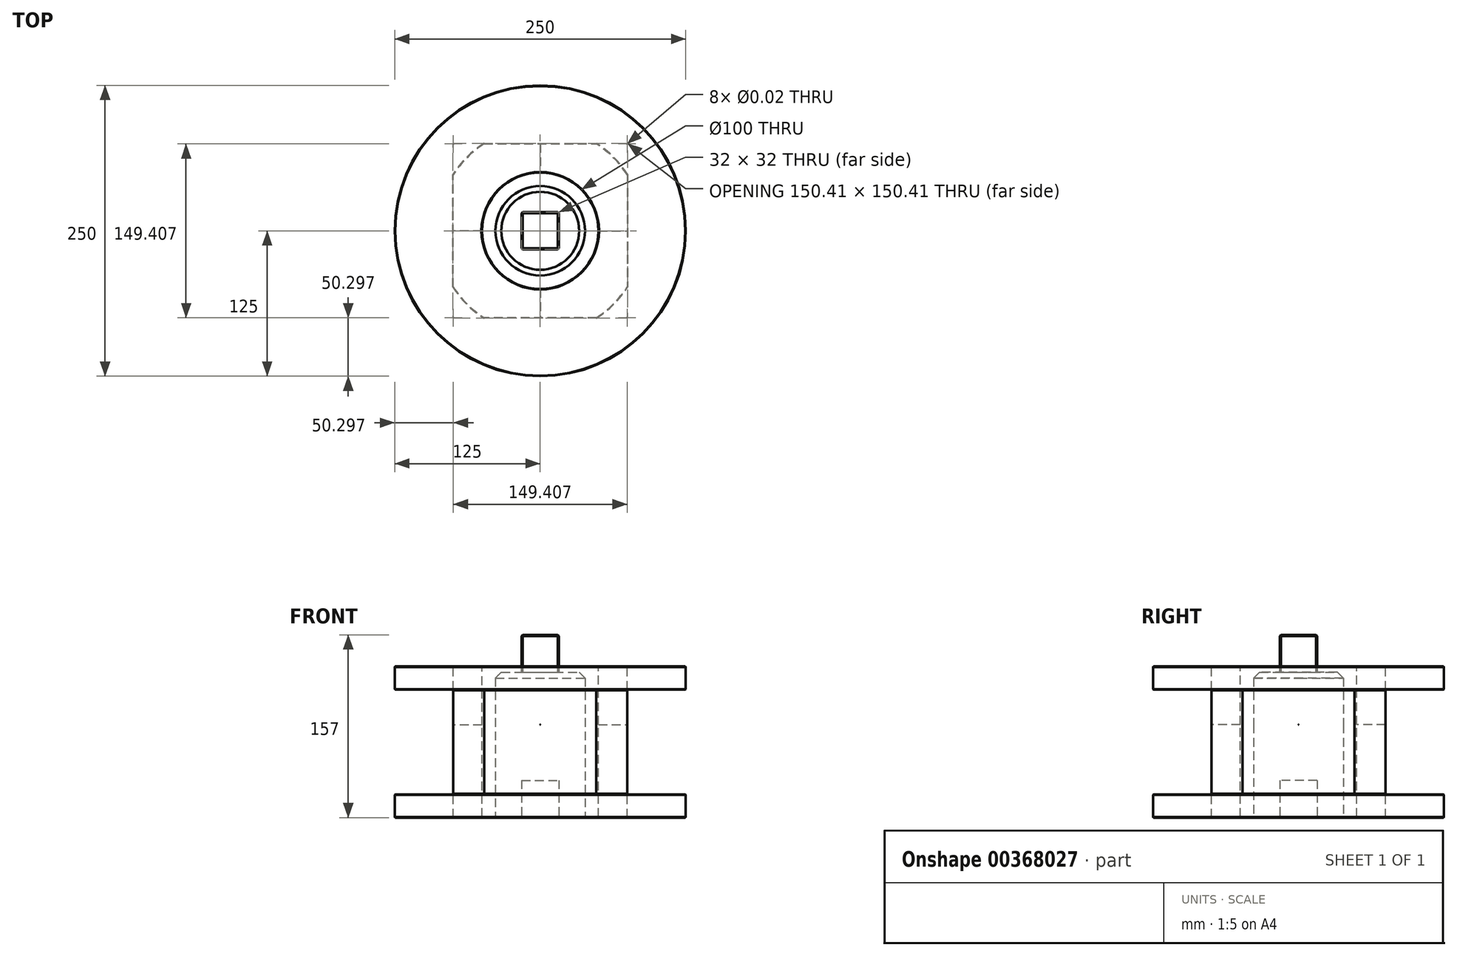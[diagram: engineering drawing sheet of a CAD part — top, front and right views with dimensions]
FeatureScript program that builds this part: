
annotation { "Feature Type Name" : "Feature", "Feature Type Description" : "" }
export const myFeature = defineFeature(function(context is Context, id is Id, definition is map)
    precondition{}
    {
        {
            var Q0;
            Q0=qCreatedBy(makeId("Top.planeOp"),FACE);
            var sketch = newSketch(context, id + "F0", { "sketchPlane" : qUnion([Q0])});
            skCircle(sketch, "E0", {"center": v(0, 0) * mm, "radius": 125 * mm});
            skCircle(sketch, "E1", {"center": v(0, 0) * mm, "radius": 50 * mm});
            skCircle(sketch, "E2.cCircle", {"center": v(0, 0) * mm, "radius": 105.65 * mm, "construction": true});
            skLineSegment(sketch, "E2.0", {"start": v(-74.7, -74.7) * mm, "end": v(-74.7, 74.7) * mm});
            skLineSegment(sketch, "E2.1", {"start": v(-74.7, 74.7) * mm, "end": v(74.7, 74.7) * mm});
            skLineSegment(sketch, "E2.2", {"start": v(74.7, 74.7) * mm, "end": v(74.7, -74.7) * mm});
            skLineSegment(sketch, "E2.3", {"start": v(74.7, -74.7) * mm, "end": v(-74.7, -74.7) * mm});
            skCircle(sketch, "E3", {"center": v(0, 0) * mm, "radius": 88.89 * mm});
            skSolve(sketch);
        }
        {
            var Q0;
            {var subQ0=sQuery(id+"F0.wireOp",EDGE,"E3");var subQ1=sQuery(id+"F0.wireOp",EDGE,"E2.3");var subQ2=makeQuery(id+"F0.imprint","INTERSECT",VERTEX,{"disambiguationData":[OD(0.0)],"derivedFrom":[subQ1,subQ0]});Q0=makeQuery(id+"F0.imprint","IMPRINT",FACE,{"disambiguationData":[TD([[makeQuery(id+"F0.imprint","IMPRINT",EDGE,{"disambiguationData":[TD([[subQ2,-1.0]])],"derivedFrom":subQ1}),1.0]])]});}
            var Q1;
            Q1=makeQuery(id+"F0.imprint","IMPRINT",FACE,{"disambiguationData":[TD([[makeQuery(id+"F0.imprint","IMPRINT",EDGE,{"derivedFrom":sQuery(id+"F0.wireOp",EDGE,"E0")}),1.0]])]});
            var Q2;
            {var subQ0=sQuery(id+"F0.wireOp",EDGE,"E3");var subQ1=sQuery(id+"F0.wireOp",EDGE,"E2.0");var subQ2=makeQuery(id+"F0.imprint","INTERSECT",VERTEX,{"disambiguationData":[OD(0.0)],"derivedFrom":[subQ1,subQ0]});Q2=makeQuery(id+"F0.imprint","IMPRINT",FACE,{"disambiguationData":[TD([[makeQuery(id+"F0.imprint","IMPRINT",EDGE,{"disambiguationData":[TD([[subQ2,-1.0]])],"derivedFrom":subQ1}),1.0]])]});}
            var Q3;
            {var subQ0=sQuery(id+"F0.wireOp",EDGE,"E3");var subQ1=sQuery(id+"F0.wireOp",EDGE,"E2.1");var subQ2=makeQuery(id+"F0.imprint","INTERSECT",VERTEX,{"disambiguationData":[OD(0.0)],"derivedFrom":[subQ1,subQ0]});Q3=makeQuery(id+"F0.imprint","IMPRINT",FACE,{"disambiguationData":[TD([[makeQuery(id+"F0.imprint","IMPRINT",EDGE,{"disambiguationData":[TD([[subQ2,-1.0]])],"derivedFrom":subQ1}),1.0]])]});}
            var Q4;
            {var subQ0=sQuery(id+"F0.wireOp",EDGE,"E2.1");var subQ1=sQuery(id+"F0.wireOp",EDGE,"E2.0");var subQ2=makeQuery(id+"F0.imprint","INTERSECT",VERTEX,{"derivedFrom":[subQ1,subQ0]});Q4=makeQuery(id+"F0.imprint","IMPRINT",FACE,{"disambiguationData":[TD([[makeQuery(id+"F0.imprint","IMPRINT",EDGE,{"disambiguationData":[TD([[subQ2,1.0]])],"derivedFrom":subQ1}),-1.0]])]});}
            var Q5;
            {var subQ0=sQuery(id+"F0.wireOp",EDGE,"E2.3");var subQ1=sQuery(id+"F0.wireOp",EDGE,"E2.0");var subQ2=makeQuery(id+"F0.imprint","INTERSECT",VERTEX,{"derivedFrom":[subQ1,subQ0]});Q5=makeQuery(id+"F0.imprint","IMPRINT",FACE,{"disambiguationData":[TD([[makeQuery(id+"F0.imprint","IMPRINT",EDGE,{"disambiguationData":[TD([[subQ2,-1.0]])],"derivedFrom":subQ1}),-1.0]])]});}
            var Q6;
            {var subQ0=sQuery(id+"F0.wireOp",EDGE,"E2.3");var subQ1=sQuery(id+"F0.wireOp",EDGE,"E2.2");var subQ2=makeQuery(id+"F0.imprint","INTERSECT",VERTEX,{"derivedFrom":[subQ1,subQ0]});Q6=makeQuery(id+"F0.imprint","IMPRINT",FACE,{"disambiguationData":[TD([[makeQuery(id+"F0.imprint","IMPRINT",EDGE,{"disambiguationData":[TD([[subQ2,1.0]])],"derivedFrom":subQ1}),-1.0]])]});}
            var Q7;
            {var subQ0=sQuery(id+"F0.wireOp",EDGE,"E3");var subQ1=sQuery(id+"F0.wireOp",EDGE,"E2.2");var subQ2=makeQuery(id+"F0.imprint","INTERSECT",VERTEX,{"disambiguationData":[OD(0.0)],"derivedFrom":[subQ1,subQ0]});Q7=makeQuery(id+"F0.imprint","IMPRINT",FACE,{"disambiguationData":[TD([[makeQuery(id+"F0.imprint","IMPRINT",EDGE,{"disambiguationData":[TD([[subQ2,-1.0]])],"derivedFrom":subQ1}),1.0]])]});}
            var Q8;
            {var subQ0=sQuery(id+"F0.wireOp",EDGE,"E2.2");var subQ1=sQuery(id+"F0.wireOp",EDGE,"E2.1");var subQ2=makeQuery(id+"F0.imprint","INTERSECT",VERTEX,{"derivedFrom":[subQ1,subQ0]});Q8=makeQuery(id+"F0.imprint","IMPRINT",FACE,{"disambiguationData":[TD([[makeQuery(id+"F0.imprint","IMPRINT",EDGE,{"disambiguationData":[TD([[subQ2,1.0]])],"derivedFrom":subQ1}),-1.0]])]});}
            var Q9;
            Q9=makeQuery(id+"F0.imprint","IMPRINT",FACE,{"disambiguationData":[TD([[makeQuery(id+"F0.imprint","IMPRINT",EDGE,{"derivedFrom":sQuery(id+"F0.wireOp",EDGE,"E1")}),-1.0]])]});
            extrude(context, id + "F1", {"entities" : qUnion([Q0, Q1, Q2, Q3, Q4, Q5, Q6, Q7, Q8, Q9]), "oppositeDirection" : true, "depth" : 20 * mm});
        }
        {
            var Q0;
            Q0=makeQuery(id+"F0.imprint","IMPRINT",FACE,{"disambiguationData":[TD([[makeQuery(id+"F0.imprint","IMPRINT",EDGE,{"derivedFrom":sQuery(id+"F0.wireOp",EDGE,"E1")}),-1.0]])]});
            extrude(context, id + "F2", {"entities" : qUnion([Q0]), "operationType" : NewBodyOperationType.ADD, "depth" : 45 * mm});
        }
        {
            var Q0;
            Q0=makeQuery(id+"F1.opExtrude","SWEPT_BODY",BODY,{"disambiguationData":[OSD([sQuery(id+"F0.wireOp",EDGE,"E0"),sQuery(id+"F0.wireOp",EDGE,"E1")])]});
            var Q1;
            Q1=makeQuery(id+"F2.opExtrude","CAP_FACE",FACE,{"disambiguationData":[OSD([sQuery(id+"F0.wireOp",EDGE,"E1"),sQuery(id+"F0.wireOp",EDGE,"E2.0"),sQuery(id+"F0.wireOp",EDGE,"E2.1"),sQuery(id+"F0.wireOp",EDGE,"E2.2"),sQuery(id+"F0.wireOp",EDGE,"E2.3"),sQuery(id+"F0.wireOp",EDGE,"E3")])],"isStart":false});
            mirror(context, id + "F3", {"operationType" : NewBodyOperationType.ADD, "entities" : qUnion([Q0]), "mirrorPlane" : qUnion([Q1])});
        }
        {
            var Q0;
            {var subQ0=makeQuery(id+"F2.opExtrude","SWEPT_FACE",FACE,{"disambiguationData":[OSD([sQuery(id+"F0.wireOp",EDGE,"E2.2")])]});Q0=makeQuery(id+"F3.boolean.opBoolean","MERGE",FACE,{"derivedFrom":[subQ0,makeQuery(id+"F3.opPattern","COPY",FACE,{"derivedFrom":subQ0,"instanceName":"1"})]});}
            var sketch = newSketch(context, id + "F4", { "sketchPlane" : qUnion([Q0])});
            skPoint(sketch, "E4", {"position": v(0, 60) * mm});
            skSolve(sketch);
        }
        {
            var Q0;
            {var subQ0=makeQuery(id+"F2.opExtrude","SWEPT_FACE",FACE,{"disambiguationData":[OSD([sQuery(id+"F0.wireOp",EDGE,"E2.3")])]});Q0=makeQuery(id+"F3.boolean.opBoolean","MERGE",FACE,{"derivedFrom":[subQ0,makeQuery(id+"F3.opPattern","COPY",FACE,{"derivedFrom":subQ0,"instanceName":"1"})]});}
            var sketch = newSketch(context, id + "F5", { "sketchPlane" : qUnion([Q0])});
            skPoint(sketch, "E5", {"position": v(0, 60) * mm});
            skPoint(sketch, "E5.positionSnap0", {"position": v(0, 0) * mm});
            skSolve(sketch);
        }
        {
            var Q0;
            Q0=makeQuery(id+"F3.opPattern","COPY",FACE,{"derivedFrom":makeQuery(id+"F1.opExtrude","CAP_FACE",FACE,{"disambiguationData":[OSD([sQuery(id+"F0.wireOp",EDGE,"E0"),sQuery(id+"F0.wireOp",EDGE,"E1")])],"isStart":false}),"instanceName":"1"});
            var sketch = newSketch(context, id + "F6", { "sketchPlane" : qUnion([Q0])});
            skPoint(sketch, "E6", {"position": v(-74.7, -74.7) * mm});
            skPoint(sketch, "E7", {"position": v(-74.7, 74.7) * mm});
            skPoint(sketch, "E8", {"position": v(74.7, 74.7) * mm});
            skPoint(sketch, "E9", {"position": v(74.7, -74.7) * mm});
            skSolve(sketch);
        }
        {
            var Q0;
            Q0=makeQuery(id+"F1.opExtrude","CAP_FACE",FACE,{"disambiguationData":[OSD([sQuery(id+"F0.wireOp",EDGE,"E0"),sQuery(id+"F0.wireOp",EDGE,"E1")])],"isStart":false});
            var sketch = newSketch(context, id + "F7", { "sketchPlane" : qUnion([Q0])});
            skCircle(sketch, "E10", {"center": v(0, 0) * mm, "radius": 38.5 * mm});
            skSolve(sketch);
        }
        {
            var Q0;
            Q0=makeQuery(id+"F7.imprint","IMPRINT",FACE,{"disambiguationData":[TD([[makeQuery(id+"F7.imprint","IMPRINT",EDGE,{"derivedFrom":sQuery(id+"F7.wireOp",EDGE,"E10")}),1.0]])]});
            extrude(context, id + "F8", {"entities" : qUnion([Q0]), "oppositeDirection" : true, "depth" : 125 * mm});
        }
        {
            var Q0;
            Q0=makeQuery(id+"F8.opExtrude","CAP_FACE",FACE,{"disambiguationData":[OSD([sQuery(id+"F7.wireOp",EDGE,"E10")])],"isStart":false});
            var sketch = newSketch(context, id + "F9", { "sketchPlane" : qUnion([Q0])});
            skLineSegment(sketch, "E11.bottom", {"start": v(-16, -16) * mm, "end": v(16, -16) * mm});
            skLineSegment(sketch, "E11.top", {"start": v(-16, 16) * mm, "end": v(16, 16) * mm});
            skLineSegment(sketch, "E11.left", {"start": v(-16, -16) * mm, "end": v(-16, 16) * mm});
            skLineSegment(sketch, "E11.right", {"start": v(16, -16) * mm, "end": v(16, 16) * mm});
            skPoint(sketch, "E11.middle", {"position": v(0, 0) * mm});
            skSolve(sketch);
        }
        {
            var Q0;
            Q0 = qSketchRegion(id + "F9", true);
            var Q1;
            Q1=makeQuery(id+"F9.imprint","IMPRINT",FACE,{"disambiguationData":[TD([[makeQuery(id+"F9.imprint","IMPRINT",EDGE,{"derivedFrom":sQuery(id+"F9.wireOp",EDGE,"E11.bottom")}),1.0]])]});
            extrude(context, id + "F10", {"entities" : qUnion([Q0, Q1]), "operationType" : NewBodyOperationType.ADD, "depth" : 32 * mm});
        }
        {
            var Q0;
            Q0=makeQuery(id+"F8.opExtrude","CAP_FACE",FACE,{"disambiguationData":[OSD([sQuery(id+"F7.wireOp",EDGE,"E10")])],"isStart":true});
            var sketch = newSketch(context, id + "F11", { "sketchPlane" : qUnion([Q0])});
            skLineSegment(sketch, "E12.bottom", {"start": v(-16, -16) * mm, "end": v(16, -16) * mm});
            skLineSegment(sketch, "E12.top", {"start": v(-16, 16) * mm, "end": v(16, 16) * mm});
            skLineSegment(sketch, "E12.left", {"start": v(-16, -16) * mm, "end": v(-16, 16) * mm});
            skLineSegment(sketch, "E12.right", {"start": v(16, -16) * mm, "end": v(16, 16) * mm});
            skPoint(sketch, "E12.middle", {"position": v(0, 0) * mm});
            skSolve(sketch);
        }
        {
            var Q0;
            Q0 = qSketchRegion(id + "F11", true);
            var Q1;
            Q1=makeQuery(id+"F11.imprint","IMPRINT",FACE,{"disambiguationData":[TD([[makeQuery(id+"F11.imprint","IMPRINT",EDGE,{"derivedFrom":sQuery(id+"F11.wireOp",EDGE,"E12.bottom")}),1.0]])]});
            extrude(context, id + "F12", {"entities" : qUnion([Q0, Q1]), "operationType" : NewBodyOperationType.REMOVE, "oppositeDirection" : true, "depth" : 32 * mm});
        }
        {
            var Q0;
            Q0=makeQuery(id+"F10.opExtrude","SWEPT_EDGE",EDGE,{"disambiguationData":[OSD([sQuery(id+"F9.wireOp",EDGE,"E11.top"),sQuery(id+"F9.wireOp",EDGE,"E11.left")])]});
            var Q1;
            Q1=makeQuery(id+"F10.opExtrude","SWEPT_EDGE",EDGE,{"disambiguationData":[OSD([sQuery(id+"F9.wireOp",EDGE,"E11.bottom"),sQuery(id+"F9.wireOp",EDGE,"E11.left")])]});
            var Q2;
            Q2=makeQuery(id+"F10.opExtrude","SWEPT_EDGE",EDGE,{"disambiguationData":[OSD([sQuery(id+"F9.wireOp",EDGE,"E11.bottom"),sQuery(id+"F9.wireOp",EDGE,"E11.right")])]});
            var Q3;
            Q3=makeQuery(id+"F10.opExtrude","CAP_FACE",FACE,{"disambiguationData":[OSD([sQuery(id+"F9.wireOp",EDGE,"E11.bottom"),sQuery(id+"F9.wireOp",EDGE,"E11.top"),sQuery(id+"F9.wireOp",EDGE,"E11.left"),sQuery(id+"F9.wireOp",EDGE,"E11.right")])],"isStart":false});
            var Q4;
            Q4=makeQuery(id+"F10.opExtrude","SWEPT_EDGE",EDGE,{"disambiguationData":[OSD([sQuery(id+"F9.wireOp",EDGE,"E11.top"),sQuery(id+"F9.wireOp",EDGE,"E11.right")])]});
            chamfer(context, id + "F13", {"entities" : qUnion([Q0, Q1, Q2, Q3, Q4]), "width" : 1 * mm, "tangentPropagation" : true});
        }
        {
            var Q0;
            Q0=makeQuery(id+"F3.opPattern","COPY",FACE,{"derivedFrom":makeQuery(id+"F1.opExtrude","CAP_FACE",FACE,{"disambiguationData":[OSD([sQuery(id+"F0.wireOp",EDGE,"E0"),sQuery(id+"F0.wireOp",EDGE,"E1")])],"isStart":false}),"instanceName":"1"});
            var Q1;
            Q1=makeQuery(id+"F3.opPattern","COPY",FACE,{"derivedFrom":makeQuery(id+"F1.opExtrude","CAP_FACE",FACE,{"disambiguationData":[OSD([sQuery(id+"F0.wireOp",EDGE,"E0"),sQuery(id+"F0.wireOp",EDGE,"E1")])],"isStart":true}),"instanceName":"1"});
            var Q2;
            Q2=makeQuery(id+"F1.opExtrude","CAP_FACE",FACE,{"disambiguationData":[OSD([sQuery(id+"F0.wireOp",EDGE,"E0"),sQuery(id+"F0.wireOp",EDGE,"E1")])],"isStart":false});
            var Q3;
            Q3=makeQuery(id+"F1.opExtrude","CAP_FACE",FACE,{"disambiguationData":[OSD([sQuery(id+"F0.wireOp",EDGE,"E0"),sQuery(id+"F0.wireOp",EDGE,"E1")])],"isStart":true});
            chamfer(context, id + "F14", {"entities" : qUnion([Q0, Q1, Q2, Q3]), "width" : .5 * mm, "tangentPropagation" : true});
        }
        {
            var Q0;
            Q0=sQuery(id+"F6.wireOp",VERTEX,"E9");
            var Q1;
            Q1=sQuery(id+"F6.wireOp",VERTEX,"E8");
            var Q2;
            Q2=sQuery(id+"F6.wireOp",VERTEX,"E7");
            var Q3;
            Q3=sQuery(id+"F6.wireOp",VERTEX,"E6");
            var Q4;
            Q4=makeQuery(id+"F1.opExtrude","SWEPT_BODY",BODY,{"disambiguationData":[OSD([sQuery(id+"F0.wireOp",EDGE,"E0"),sQuery(id+"F0.wireOp",EDGE,"E1")])]});
            hole(context, id + "F15", {"style" : HoleStyle.SIMPLE, "endStyle" : HoleEndStyle.THROUGH, "standardTappedOrClearance" : lookupTablePath({ "standard" : "ANSI", "size" : "5/8 (0.62)", "type" : "Drilled" }), "standardBlindInLast" : lookupTablePath({ "standard" : "ANSI", "size" : "5/8", "type" : "Drilled" }), "holeDiameter" : 5 / 203.2 * mm, "isTappedThrough" : true, "tappedDepth" : 36.19 * mm, "tapClearance" : 3, "locations" : qUnion([Q0, Q1, Q2, Q3]), "scope" : qUnion([Q4])});
        }
        {
            var Q0;
            Q0=sQuery(id+"F5.wireOp",VERTEX,"E5");
            var Q1;
            Q1=makeQuery(id+"F1.opExtrude","SWEPT_BODY",BODY,{"disambiguationData":[OSD([sQuery(id+"F0.wireOp",EDGE,"E0"),sQuery(id+"F0.wireOp",EDGE,"E1")])]});
            var Q2;
            Q2=makeQuery(id+"F8.opExtrude","SWEPT_BODY",BODY,{"disambiguationData":[OSD([sQuery(id+"F7.wireOp",EDGE,"E10")])]});
            hole(context, id + "F16", {"style" : HoleStyle.SIMPLE, "endStyle" : HoleEndStyle.THROUGH, "standardTappedOrClearance" : lookupTablePath({ "standard" : "ANSI", "size" : "3/4 (0.75)", "type" : "Drilled" }), "standardBlindInLast" : lookupTablePath({ "standard" : "ANSI", "size" : "3/4", "type" : "Drilled" }), "holeDiameter" : 3 / 101.6 * mm, "isTappedThrough" : true, "tappedDepth" : 36.19 * mm, "tapClearance" : 3, "locations" : qUnion([Q0]), "scope" : qUnion([Q1, Q2])});
        }
        {
            var Q0;
            Q0=sQuery(id+"F4.wireOp",VERTEX,"E4");
            var Q1;
            Q1=makeQuery(id+"F1.opExtrude","SWEPT_BODY",BODY,{"disambiguationData":[OSD([sQuery(id+"F0.wireOp",EDGE,"E0"),sQuery(id+"F0.wireOp",EDGE,"E1")])]});
            hole(context, id + "F17", {"style" : HoleStyle.SIMPLE, "endStyle" : HoleEndStyle.BLIND, "standardTappedOrClearance" : lookupTablePath({ "standard" : "ANSI", "size" : "3/4 (0.75)", "type" : "Drilled" }), "standardBlindInLast" : lookupTablePath({ "standard" : "ANSI", "size" : "3/4", "type" : "Drilled" }), "holeDiameter" : 3 / 101.6 * mm, "holeDepth" : 30 * mm, "isTappedThrough" : true, "tappedDepth" : 36.19 * mm, "tapClearance" : 3, "locations" : qUnion([Q0]), "scope" : qUnion([Q1])});
        }
        {
            var Q0;
            {var subQ0=makeQuery(id+"F2.opExtrude","SWEPT_FACE",FACE,{"disambiguationData":[OSD([sQuery(id+"F0.wireOp",EDGE,"E2.0")])]});Q0=makeQuery(id+"F3.boolean.opBoolean","MERGE",FACE,{"derivedFrom":[subQ0,makeQuery(id+"F3.opPattern","COPY",FACE,{"derivedFrom":subQ0,"instanceName":"1"})]});}
            var sketch = newSketch(context, id + "F18", { "sketchPlane" : qUnion([Q0])});
            skPoint(sketch, "E13", {"position": v(0, 59.5) * mm});
            skSolve(sketch);
        }
        {
            var Q0;
            Q0=sQuery(id+"F18.wireOp",VERTEX,"E13");
            var Q1;
            Q1=makeQuery(id+"F1.opExtrude","SWEPT_BODY",BODY,{"disambiguationData":[OSD([sQuery(id+"F0.wireOp",EDGE,"E0"),sQuery(id+"F0.wireOp",EDGE,"E1")])]});
            hole(context, id + "F19", {"style" : HoleStyle.SIMPLE, "endStyle" : HoleEndStyle.BLIND, "standardTappedOrClearance" : lookupTablePath({ "standard" : "ANSI", "size" : "3/4 (0.75)", "type" : "Drilled" }), "standardBlindInLast" : lookupTablePath({ "standard" : "ANSI", "size" : "3/4", "type" : "Drilled" }), "holeDiameter" : 3 / 101.6 * mm, "holeDepth" : 30 * mm, "isTappedThrough" : true, "tappedDepth" : 36.19 * mm, "tapClearance" : 3, "locations" : qUnion([Q0]), "scope" : qUnion([Q1])});
        }
        {
            var Q0;
            Q0=makeQuery(id+"F8.opExtrude","CAP_EDGE",EDGE,{"disambiguationData":[OSD([sQuery(id+"F7.wireOp",EDGE,"E10")])],"isStart":false});
            chamfer(context, id + "F20", {"entities" : qUnion([Q0]), "width" : 5 * mm, "tangentPropagation" : true});
        }
    });
